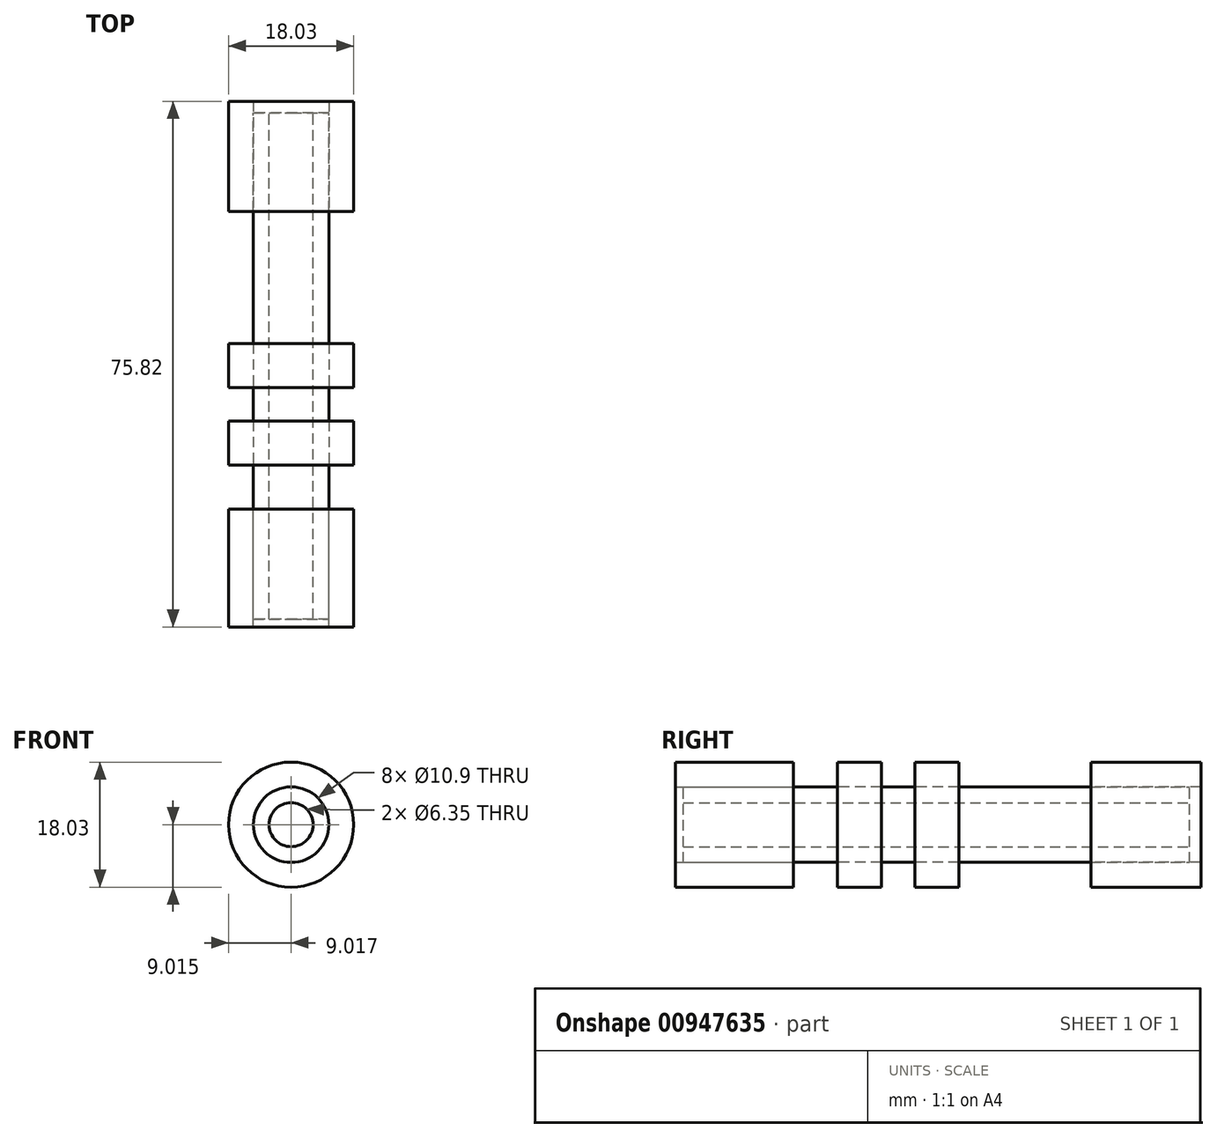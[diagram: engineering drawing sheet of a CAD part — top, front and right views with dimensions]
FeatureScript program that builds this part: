
annotation { "Feature Type Name" : "Feature", "Feature Type Description" : "" }
export const myFeature = defineFeature(function(context is Context, id is Id, definition is map)
    precondition{}
    {
        {
            var Q0;
            Q0=qCreatedBy(makeId("Front.planeOp"),FACE);
            var sketch = newSketch(context, id + "F0", { "sketchPlane" : qUnion([Q0])});
            skCircle(sketch, "E0", {"center": v(-49.54, 25.66) * mm, "radius": 9.02 * mm});
            skCircle(sketch, "E1", {"center": v(-49.54, 25.66) * mm, "radius": 5.45 * mm});
            skCircle(sketch, "E2", {"center": v(-49.54, 25.66) * mm, "radius": 3.18 * mm});
            skSolve(sketch);
        }
        {
            var Q0;
            Q0=makeQuery(id+"F0.imprint","IMPRINT",FACE,{"disambiguationData":[TD([[makeQuery(id+"F0.imprint","IMPRINT",EDGE,{"derivedFrom":sQuery(id+"F0.wireOp",EDGE,"E0")}),1.0]])]});
            extrude(context, id + "F1", {"entities" : qUnion([Q0]), "depth" : 17.02 * mm, "offsetDistance" : 25.4 * mm});
        }
        {
            var Q0;
            Q0=sQuery(id+"F0.wireOp",EDGE,"E1");
            extrude(context, id + "F2", {"bodyType" : ToolBodyType.SURFACE, "surfaceEntities" : qUnion([Q0]), "depth" : 15.88 * mm, "offsetDistance" : 25.4 * mm, "hasSecondDirection" : true, "secondDirectionOppositeDirection" : true, "secondDirectionDepth" : 59.05 * mm});
        }
        {
            var Q0;
            Q0=makeQuery(id+"F0.imprint","IMPRINT",FACE,{"disambiguationData":[TD([[makeQuery(id+"F0.imprint","IMPRINT",EDGE,{"derivedFrom":sQuery(id+"F0.wireOp",EDGE,"E0")}),1.0]])]});
            extrude(context, id + "F3", {"entities" : qUnion([Q0]), "depth" : -6.35 * mm, "offsetDistance" : 25.4 * mm});
        }
        {
            var Q0;
            Q0=makeQuery(id+"F3.opExtrude","SWEPT_BODY",BODY,{"disambiguationData":[OSD([sQuery(id+"F0.wireOp",EDGE,"E0"),sQuery(id+"F0.wireOp",EDGE,"E1")])]});
            transform(context, id + "F4", {"entities" : qUnion([Q0]), "transformType" : TransformType.TRANSLATION_3D, "dx" : 0 * mm, "dy" : 6.35 * mm, "dz" : 0 * mm, "makeCopy" : false});
        }
        {
            var Q0;
            Q0=makeQuery(id+"F3.opExtrude","CAP_FACE",FACE,{"disambiguationData":[OSD([sQuery(id+"F0.wireOp",EDGE,"E0"),sQuery(id+"F0.wireOp",EDGE,"E1")])],"isStart":false});
            extrude(context, id + "F5", {"entities" : qUnion([Q0]), "depth" : 6.35 * mm, "offsetDistance" : 25.4 * mm});
        }
        {
            var Q0;
            Q0=makeQuery(id+"F5.opExtrude","SWEPT_BODY",BODY,{"disambiguationData":[OSD([sQuery(id+"F0.wireOp",EDGE,"E0"),sQuery(id+"F0.wireOp",EDGE,"E1")])]});
            transform(context, id + "F6", {"entities" : qUnion([Q0]), "transformType" : TransformType.TRANSLATION_3D, "dx" : 0 * mm, "dy" : 4.83 * mm, "dz" : 0 * mm, "makeCopy" : false});
        }
        {
            var Q0;
            Q0=makeQuery(id+"F5.opExtrude","CAP_FACE",FACE,{"disambiguationData":[OSD([sQuery(id+"F0.wireOp",EDGE,"E0"),sQuery(id+"F0.wireOp",EDGE,"E1")])],"isStart":false});
            extrude(context, id + "F7", {"entities" : qUnion([Q0]), "depth" : 15.88 * mm, "offsetDistance" : 25.4 * mm});
        }
        {
            var Q0;
            Q0=makeQuery(id+"F7.opExtrude","SWEPT_BODY",BODY,{"disambiguationData":[OSD([sQuery(id+"F0.wireOp",EDGE,"E0"),sQuery(id+"F0.wireOp",EDGE,"E1")])]});
            transform(context, id + "F8", {"entities" : qUnion([Q0]), "transformType" : TransformType.TRANSLATION_3D, "dx" : 0 * mm, "dy" : 19.05 * mm, "dz" : 0 * mm, "makeCopy" : false});
        }
        {
            var Q0;
            Q0=makeQuery(id+"F0.imprint","IMPRINT",FACE,{"disambiguationData":[TD([[makeQuery(id+"F0.imprint","IMPRINT",EDGE,{"derivedFrom":sQuery(id+"F0.wireOp",EDGE,"E1")}),1.0]])]});
            extrude(context, id + "F9", {"entities" : qUnion([Q0]), "depth" : 15.88 * mm, "offsetDistance" : 25.4 * mm, "hasSecondDirection" : true, "secondDirectionOppositeDirection" : true, "secondDirectionDepth" : 57.15 * mm});
        }
    });
